# Revit family: Unico DE_Anta Singola
name_source: partatom
category: Doors
revit_build: Autodesk Revit 2018 (Build: 20170223_1515(x64)
units: mm (PartAtom-declared; Revit-internal decimal feet)

## family parameters
Always vertical = Yes
Cut with Voids When Loaded = No
Host = Wall
OmniClass Number = 23.30.10.00
OmniClass Title = Doors
Room Calculation Point = Yes
Shared = No

## types (18) — shared parameters
AUTORE BIM = SKEIN BIM
Analytic Construction = <Nessuno>
DIMENSIONI DISPONIBILI = https://www.eclisse.it
DOOR DIMENSIONS = For the exact door panel width DW, please refer to the technical data sheet
Function = Interior
IFC Classification = Door
ISTRUZIONI INSTALLAZIONE = https://www.eclisse.it
Manufacturer = ECLISSE
Masterformat 2014 Code = 08 10 00
Masterformat 2014 Description = Doors and Frames
Model = ECLISSE UNICO
NBS Reference Code = 59-23
NBS Reference Description = Doorsets
OmniClass Code = 23-17 11 00
OmniClass Description = Doors
SCHEDA PRODOTTO = https://www.eclisse.it
SCHEDA TECNICA = https://www.eclisse.it
UNSPSC Code = 301715
URL = https://www.eclisse.it
Uniclass 1.4 Code = L411
Uniclass 1.4 Description = Doors
Uniclass 2.0 Description = Doorsets
Uniclass 2015 Code = EF_25_30
Uniclass 2015 Name = Doors and windows
Uniformat II Code = C1020
Uniformat II Description = Interior Doors
VOCE DI CAPITOLATO = https://www.eclisse.it
Wall Closure = By host

## per-type parameters (varying)
| type | A | B | C | H1 | HP | Height | L | LE | LP | Rough Height | Rough Width | Thickness | Width | X |
| 1110X1985 | 1135 mm  [stored 3.72375 ft] | 1110 mm  [stored 3.64173 ft] | 2272 mm | 2065 mm  [stored 6.77493 ft] | 1985 mm  [stored 6.51247 ft] | 1975 mm  [stored 6.47966 ft] | 1080 mm  [stored 3.54331 ft] | 2245 mm | 1110 mm  [stored 3.64173 ft] | 2014 mm | 686 mm | 44 mm  [stored 0.144357 ft] | 1110 mm  [stored 3.64173 ft] | 466 mm |
| 1235X1985 | 1260 mm  [stored 4.13386 ft] | 1235 mm  [stored 4.05184 ft] | 2522 mm | 2065 mm  [stored 6.77493 ft] | 1985 mm  [stored 6.51247 ft] | 1975 mm  [stored 6.47966 ft] | 1205 mm  [stored 3.95341 ft] | 2495 mm | 1235 mm  [stored 4.05184 ft] | 2014 mm | 686 mm | 44 mm  [stored 0.144357 ft] | 1235 mm  [stored 4.05184 ft] | 466 mm |
| 1110X2110 | 1135 mm  [stored 3.72375 ft] | 1110 mm  [stored 3.64173 ft] | 2272 mm | 2190 mm | 2110 mm  [stored 6.92257 ft] | 2100 mm | 1080 mm  [stored 3.54331 ft] | 2245 mm | 1110 mm  [stored 3.64173 ft] | 2116 mm | 584 mm | 44 mm  [stored 0.144357 ft] | 1110 mm  [stored 3.64173 ft] | 498 mm |
| 1110X2235 | 1135 mm  [stored 3.72375 ft] | 1110 mm  [stored 3.64173 ft] | 2272 mm | 2315 mm | 2235 mm | 2225 mm | 1080 mm  [stored 3.54331 ft] | 2245 mm | 1110 mm  [stored 3.64173 ft] | 2420 mm | 584 mm | 40 mm  [stored 0.131234 ft] | 1110 mm  [stored 3.64173 ft] | 529 mm |
| 1235X2110 | 1260 mm  [stored 4.13386 ft] | 1235 mm  [stored 4.05184 ft] | 2522 mm | 2190 mm | 2110 mm  [stored 6.92257 ft] | 2100 mm | 1205 mm  [stored 3.95341 ft] | 2495 mm | 1235 mm  [stored 4.05184 ft] | 2014 mm | 686 mm | 44 mm  [stored 0.144357 ft] | 1235 mm  [stored 4.05184 ft] | 498 mm |
| 1235X2235 | 1260 mm  [stored 4.13386 ft] | 1235 mm  [stored 4.05184 ft] | 2522 mm | 2315 mm | 2235 mm | 2225 mm | 1205 mm  [stored 3.95341 ft] | 2495 mm | 1235 mm  [stored 4.05184 ft] | 2014 mm | 686 mm | 44 mm  [stored 0.144357 ft] | 1235 mm  [stored 4.05184 ft] | 529 mm |
| 610X1985 | 635 mm | 610 mm  [stored 2.00131 ft] | 1272 mm  [stored 4.17323 ft] | 2065 mm  [stored 6.77493 ft] | 1985 mm  [stored 6.51247 ft] | 1975 mm  [stored 6.47966 ft] | 580 mm | 1245 mm | 610 mm  [stored 2.00131 ft] | 2014 mm | 686 mm | 44 mm  [stored 0.144357 ft] | 610 mm  [stored 2.00131 ft] | 466 mm |
| 610X2110 | 635 mm | 610 mm  [stored 2.00131 ft] | 1272 mm  [stored 4.17323 ft] | 2190 mm | 2110 mm  [stored 6.92257 ft] | 2100 mm | 580 mm | 1245 mm | 610 mm  [stored 2.00131 ft] | 2014 mm | 686 mm | 44 mm  [stored 0.144357 ft] | 610 mm  [stored 2.00131 ft] | 498 mm |
| 610X2235 | 635 mm | 610 mm  [stored 2.00131 ft] | 1272 mm  [stored 4.17323 ft] | 2315 mm | 2235 mm | 2225 mm | 580 mm | 1245 mm | 610 mm  [stored 2.00131 ft] | 2014 mm | 686 mm | 44 mm  [stored 0.144357 ft] | 610 mm  [stored 2.00131 ft] | 529 mm |
| 735X1985 | 760 mm | 735 mm | 1522 mm  [stored 4.99344 ft] | 2065 mm  [stored 6.77493 ft] | 1985 mm  [stored 6.51247 ft] | 1975 mm  [stored 6.47966 ft] | 705 mm | 1495 mm | 735 mm | 2014 mm | 686 mm | 44 mm  [stored 0.144357 ft] | 735 mm | 466 mm |
| 735X2110 | 760 mm | 735 mm | 1522 mm  [stored 4.99344 ft] | 2190 mm | 2110 mm  [stored 6.92257 ft] | 2100 mm | 705 mm | 1495 mm | 735 mm | 2014 mm | 686 mm | 44 mm  [stored 0.144357 ft] | 735 mm | 498 mm |
| 735X2235 | 760 mm | 735 mm | 1522 mm  [stored 4.99344 ft] | 2315 mm | 2235 mm | 2225 mm | 705 mm | 1495 mm | 735 mm | 2014 mm | 686 mm | 44 mm  [stored 0.144357 ft] | 735 mm | 529 mm |
| 860X1985 | 885 mm | 860 mm | 1772 mm  [stored 5.81365 ft] | 2065 mm  [stored 6.77493 ft] | 1985 mm  [stored 6.51247 ft] | 1975 mm  [stored 6.47966 ft] | 830 mm | 1745 mm | 860 mm | 2014 mm | 686 mm | 44 mm  [stored 0.144357 ft] | 860 mm | 466 mm |
| 860X2110 | 885 mm | 860 mm | 1772 mm  [stored 5.81365 ft] | 2190 mm | 2110 mm  [stored 6.92257 ft] | 2100 mm | 830 mm | 1745 mm | 860 mm | 2014 mm | 686 mm | 44 mm  [stored 0.144357 ft] | 860 mm | 498 mm |
| 860X2235 | 885 mm | 860 mm | 1772 mm  [stored 5.81365 ft] | 2315 mm | 2235 mm | 2225 mm | 830 mm | 1745 mm | 860 mm | 2014 mm | 686 mm | 44 mm  [stored 0.144357 ft] | 860 mm | 529 mm |
| 985X1985 | 1010 mm  [stored 3.31365 ft] | 985 mm  [stored 3.23163 ft] | 2022 mm  [stored 6.63386 ft] | 2065 mm  [stored 6.77493 ft] | 1985 mm  [stored 6.51247 ft] | 1975 mm  [stored 6.47966 ft] | 955 mm  [stored 3.1332 ft] | 1995 mm  [stored 6.54528 ft] | 985 mm  [stored 3.23163 ft] | 2014 mm | 686 mm | 44 mm  [stored 0.144357 ft] | 985 mm  [stored 3.23163 ft] | 466 mm |
| 985X2110 | 1010 mm  [stored 3.31365 ft] | 985 mm  [stored 3.23163 ft] | 2022 mm  [stored 6.63386 ft] | 2190 mm | 2110 mm  [stored 6.92257 ft] | 2100 mm | 955 mm  [stored 3.1332 ft] | 1995 mm  [stored 6.54528 ft] | 985 mm  [stored 3.23163 ft] | 2014 mm | 686 mm | 44 mm  [stored 0.144357 ft] | 985 mm  [stored 3.23163 ft] | 498 mm |
| 985X2235 | 1010 mm  [stored 3.31365 ft] | 985 mm  [stored 3.23163 ft] | 2022 mm  [stored 6.63386 ft] | 2315 mm | 2235 mm | 2225 mm | 955 mm  [stored 3.1332 ft] | 1995 mm  [stored 6.54528 ft] | 985 mm  [stored 3.23163 ft] | 2014 mm | 686 mm | 44 mm  [stored 0.144357 ft] | 985 mm  [stored 3.23163 ft] | 529 mm |

note: [stored X ft] marks values corroborated as IEEE doubles in the binary element streams (Revit-internal decimal feet)

## geometry (parser evidence)
native form markers: Blend x4, Sweep x10
no freeform markers — native parametric forms only
